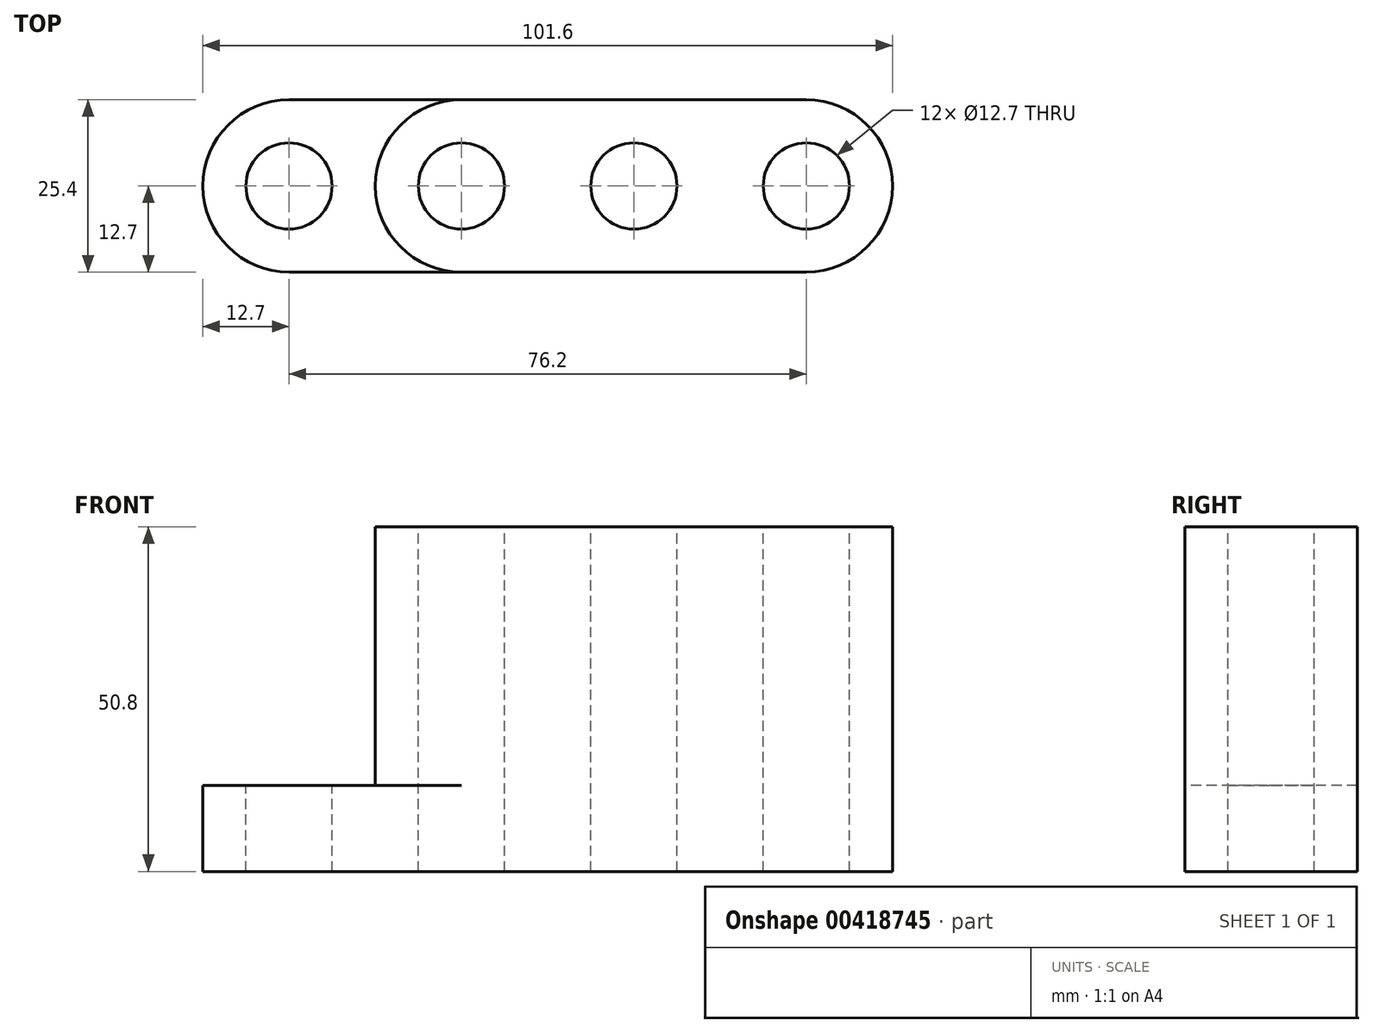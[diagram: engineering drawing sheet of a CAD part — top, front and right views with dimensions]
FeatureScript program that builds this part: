
annotation { "Feature Type Name" : "Feature", "Feature Type Description" : "" }
export const myFeature = defineFeature(function(context is Context, id is Id, definition is map)
    precondition{}
    {
        {
            var Q0;
            Q0=qCreatedBy(makeId("Front.planeOp"),FACE);
            var sketch = newSketch(context, id + "F0", { "sketchPlane" : qUnion([Q0])});
            skLineSegment(sketch, "E0", {"start": v(0, 0) * mm, "end": v(101.6, 0) * mm});
            skLineSegment(sketch, "E1", {"start": v(101.6, 0) * mm, "end": v(101.6, 50.8) * mm});
            skLineSegment(sketch, "E2", {"start": v(101.6, 50.8) * mm, "end": v(0, 50.8) * mm});
            skLineSegment(sketch, "E3", {"start": v(0, 50.8) * mm, "end": v(0, 0) * mm});
            skSolve(sketch);
        }
        {
            var Q0;
            Q0 = qSketchRegion(id + "F0", true);
            extrude(context, id + "F1", {"entities" : qUnion([Q0]), "depth" : 25.4 * mm});
        }
        {
            var Q0;
            Q0=makeQuery(id+"F1.opExtrude","SWEPT_FACE",FACE,{"disambiguationData":[OSD([sQuery(id+"F0.wireOp",EDGE,"E2")])]});
            var sketch = newSketch(context, id + "F2", { "sketchPlane" : qUnion([Q0])});
            skCircle(sketch, "E4", {"center": v(12.7, -12.7) * mm, "radius": 6.35 * mm});
            skPoint(sketch, "E4.centerSnap0", {"position": v(0, -12.7) * mm});
            skArc(sketch, "E5", {"start": v(12.7, 0) * mm, "mid": v(0, -12.7) * mm, "end": v(12.7, -25.4) * mm});
            skArc(sketch, "E6", {"start": v(12.7, -25.4) * mm, "mid": v(25.4, -12.7) * mm, "end": v(12.7, 0) * mm});
            skCircle(sketch, "E7", {"center": v(38.1, -12.7) * mm, "radius": 12.7 * mm});
            skPoint(sketch, "E7.centerSnap0", {"position": v(25.4, -12.7) * mm});
            skCircle(sketch, "E8", {"center": v(38.1, -12.7) * mm, "radius": 6.35 * mm});
            skCircle(sketch, "E9", {"center": v(63.5, -12.7) * mm, "radius": 6.35 * mm});
            skPoint(sketch, "E9.centerSnap0", {"position": v(101.6, -12.7) * mm});
            skCircle(sketch, "E10", {"center": v(88.9, -12.7) * mm, "radius": 6.35 * mm});
            skLineSegment(sketch, "E11", {"start": v(63.49, -19.05) * mm, "end": v(88.89, -19.05) * mm});
            skLineSegment(sketch, "E12", {"start": v(63.49, -6.35) * mm, "end": v(88.89, -6.35) * mm});
            skArc(sketch, "E13", {"start": v(88.89, -25.4) * mm, "mid": v(101.6, -12.7) * mm, "end": v(88.89, 0) * mm});
            skSolve(sketch);
        }
        {
            var Q0;
            Q0=makeQuery(id+"F2.imprint","IMPRINT",FACE,{"disambiguationData":[TD([[makeQuery(id+"F2.imprint","IMPRINT",EDGE,{"derivedFrom":sQuery(id+"F2.wireOp",EDGE,"E4")}),1.0]])]});
            var Q1;
            Q1=makeQuery(id+"F2.imprint","IMPRINT",FACE,{"disambiguationData":[TD([[makeQuery(id+"F2.imprint","IMPRINT",EDGE,{"derivedFrom":sQuery(id+"F2.wireOp",EDGE,"E8")}),1.0]])]});
            var Q2;
            {var subQ0=sQuery(id+"F2.wireOp",EDGE,"E5");var subQ1=sQuery(id+"F0.wireOp",EDGE,"E2");var subQ2=makeQuery(id+"F1.opExtrude","CAP_EDGE",EDGE,{"disambiguationData":[OSD([subQ1])],"isStart":false});var subQ3=makeQuery(id+"F2.imprint","INTERSECT",VERTEX,{"derivedFrom":[subQ2,subQ0,sQuery(id+"F2.wireOp",EDGE,"E6")]});Q2=makeQuery(id+"F2.imprint","IMPRINT",FACE,{"disambiguationData":[TD([[makeQuery(id+"F2.imprint","IMPRINT",EDGE,{"disambiguationData":[TD([[subQ3,1.0]])],"derivedFrom":subQ0}),-1.0]])]});}
            var Q3;
            {var subQ0=sQuery(id+"F2.wireOp",EDGE,"E5");var subQ1=sQuery(id+"F0.wireOp",EDGE,"E2");var subQ2=makeQuery(id+"F1.opExtrude","CAP_EDGE",EDGE,{"disambiguationData":[OSD([subQ1])],"isStart":true});var subQ3=makeQuery(id+"F2.imprint","INTERSECT",VERTEX,{"derivedFrom":[subQ2,subQ0,sQuery(id+"F2.wireOp",EDGE,"E6")]});Q3=makeQuery(id+"F2.imprint","IMPRINT",FACE,{"disambiguationData":[TD([[makeQuery(id+"F2.imprint","IMPRINT",EDGE,{"disambiguationData":[TD([[subQ3,-1.0]])],"derivedFrom":subQ0}),-1.0]])]});}
            var Q4;
            {var subQ0=sQuery(id+"F2.wireOp",EDGE,"E9");var subQ2=makeQuery(id+"F2.imprint","IMPRINT",VERTEX,{"disambiguationData":[OD(0.0)],"derivedFrom":subQ0});Q4=makeQuery(id+"F2.imprint","IMPRINT",FACE,{"disambiguationData":[TD([[makeQuery(id+"F2.imprint","IMPRINT",EDGE,{"disambiguationData":[TD([[subQ2,-1.0]])],"derivedFrom":subQ0}),1.0]])]});}
            var Q5;
            {var subQ0=sQuery(id+"F2.wireOp",EDGE,"E11");Q5=makeQuery(id+"F2.imprint","IMPRINT",FACE,{"disambiguationData":[TD([[makeQuery(id+"F2.imprint","IMPRINT",EDGE,{"derivedFrom":subQ0}),1.0]])]});}
            var Q6;
            {var subQ0=sQuery(id+"F2.wireOp",EDGE,"E10");var subQ1=makeQuery(id+"F2.imprint","INTERSECT",VERTEX,{"derivedFrom":[subQ0,sQuery(id+"F2.wireOp",EDGE,"E11")]});Q6=makeQuery(id+"F2.imprint","IMPRINT",FACE,{"disambiguationData":[TD([[makeQuery(id+"F2.imprint","IMPRINT",EDGE,{"disambiguationData":[TD([[subQ1,1.0]])],"derivedFrom":subQ0}),1.0]])]});}
            var Q7;
            {var subQ0=sQuery(id+"F2.wireOp",EDGE,"E13");var subQ1=sQuery(id+"F0.wireOp",EDGE,"E2");var subQ2=makeQuery(id+"F1.opExtrude","CAP_EDGE",EDGE,{"disambiguationData":[OSD([subQ1])],"isStart":true});var subQ3=makeQuery(id+"F2.imprint","INTERSECT",VERTEX,{"derivedFrom":[subQ2,subQ0]});Q7=makeQuery(id+"F2.imprint","IMPRINT",FACE,{"disambiguationData":[TD([[makeQuery(id+"F2.imprint","IMPRINT",EDGE,{"disambiguationData":[TD([[subQ3,1.0]])],"derivedFrom":subQ0}),-1.0]])]});}
            var Q8;
            {var subQ0=sQuery(id+"F2.wireOp",EDGE,"E13");var subQ1=sQuery(id+"F0.wireOp",EDGE,"E2");var subQ4=makeQuery(id+"F1.opExtrude","SWEPT_EDGE",EDGE,{"disambiguationData":[OSD([sQuery(id+"F0.wireOp",EDGE,"E1"),subQ1])]});var subQ5=makeQuery(id+"F2.imprint","INTERSECT",VERTEX,{"derivedFrom":[subQ4,subQ0]});Q8=makeQuery(id+"F2.imprint","IMPRINT",FACE,{"disambiguationData":[TD([[makeQuery(id+"F2.imprint","IMPRINT",EDGE,{"disambiguationData":[TD([[subQ5,1.0]])],"derivedFrom":subQ0}),-1.0]])]});}
            extrude(context, id + "F3", {"entities" : qUnion([Q0, Q1, Q2, Q3, Q4, Q5, Q6, Q7, Q8]), "operationType" : NewBodyOperationType.REMOVE, "oppositeDirection" : true, "depth" : 304.8 * mm});
        }
        {
            var Q0;
            Q0=makeQuery(id+"F2.imprint","IMPRINT",FACE,{"disambiguationData":[TD([[makeQuery(id+"F2.imprint","IMPRINT",EDGE,{"derivedFrom":sQuery(id+"F2.wireOp",EDGE,"E4")}),-1.0]])]});
            var Q1;
            {var subQ0=sQuery(id+"F2.wireOp",EDGE,"E6");var subQ3=sQuery(id+"F2.wireOp",EDGE,"E7");var subQ4=makeQuery(id+"F2.imprint","INTERSECT",VERTEX,{"derivedFrom":[subQ0,subQ3]});Q1=makeQuery(id+"F2.imprint","IMPRINT",FACE,{"disambiguationData":[TD([[makeQuery(id+"F2.imprint","IMPRINT",EDGE,{"disambiguationData":[TD([[subQ4,1.0]])],"derivedFrom":subQ0}),-1.0]])]});}
            var Q2;
            {var subQ0=sQuery(id+"F2.wireOp",EDGE,"E6");var subQ3=sQuery(id+"F2.wireOp",EDGE,"E7");var subQ4=makeQuery(id+"F2.imprint","INTERSECT",VERTEX,{"derivedFrom":[subQ0,subQ3]});Q2=makeQuery(id+"F2.imprint","IMPRINT",FACE,{"disambiguationData":[TD([[makeQuery(id+"F2.imprint","IMPRINT",EDGE,{"disambiguationData":[TD([[subQ4,-1.0]])],"derivedFrom":subQ0}),-1.0]])]});}
            var Q3;
            {var subQ10=sQuery(id+"F2.wireOp",EDGE,"E11");Q3=makeQuery(id+"F2.imprint","IMPRINT",FACE,{"disambiguationData":[TD([[makeQuery(id+"F2.imprint","IMPRINT",EDGE,{"derivedFrom":subQ10}),-1.0]])]});}
            extrude(context, id + "F4", {"entities" : qUnion([Q0, Q1, Q2, Q3]), "operationType" : NewBodyOperationType.REMOVE, "oppositeDirection" : true, "depth" : 38.1 * mm});
        }
    });
